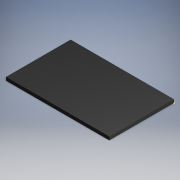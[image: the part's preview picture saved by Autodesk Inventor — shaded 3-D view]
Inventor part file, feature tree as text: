
AUTODESK INVENTOR PART (.ipt)
format: ipt  version: 2018 (Build 220112000, 112)  size: 92,672 bytes
history: native  units: in
note: dims shown in document units (in); Inventor stores cm internally (conversion verified against a paired STEP export)
features: sketch x2, extrude x1
ambient origin geometry x8: Origin, YZ Plane, XZ Plane, XY Plane, X Axis, Y Axis, Z Axis, Center Point
bodies: Solid1 (feature_tree)
feature tree (3):
  sketch  "Sketch1"  dims[d0=4.7835in d1=2.9921in]
  extrude  "Extrusion1"  Depth=2.9921in
  sketch  "Sketch2"  dims[d2=0.1555in d3=0.0in]
